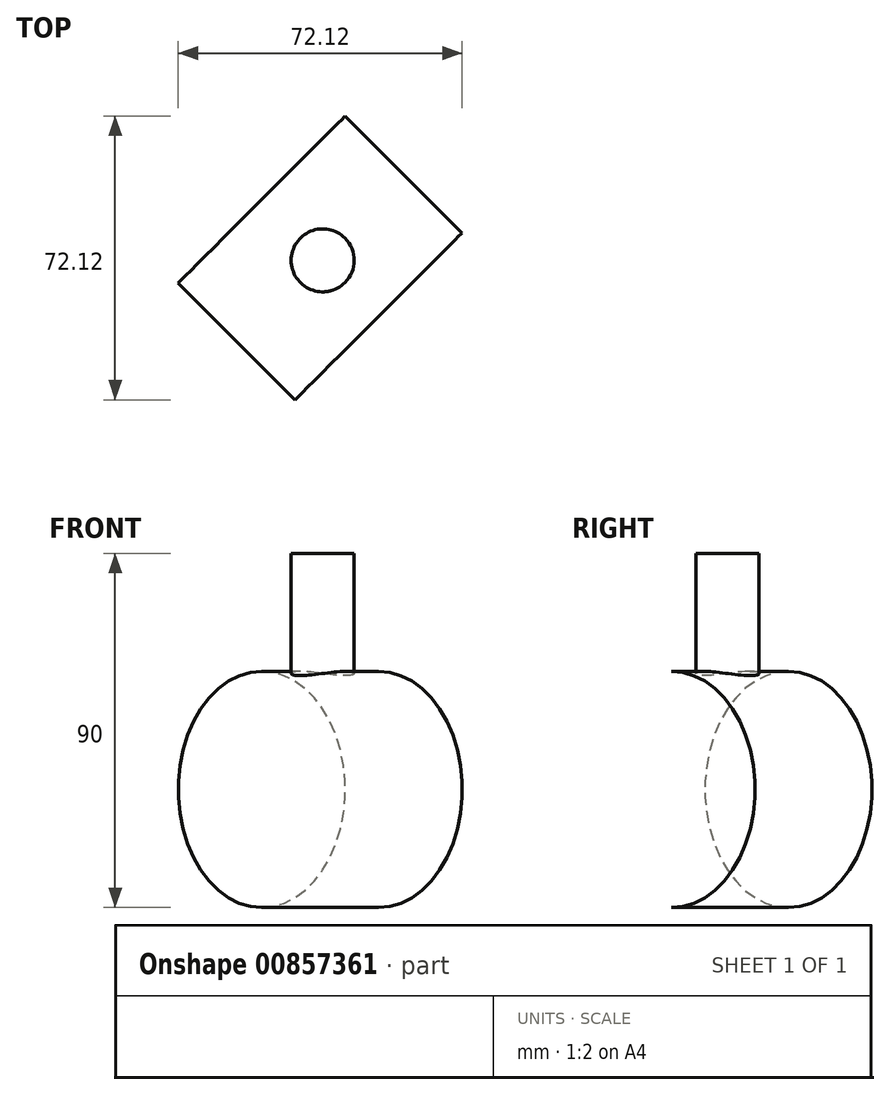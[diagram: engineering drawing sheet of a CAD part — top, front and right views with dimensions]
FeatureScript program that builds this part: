
annotation { "Feature Type Name" : "Feature", "Feature Type Description" : "" }
export const myFeature = defineFeature(function(context is Context, id is Id, definition is map)
    precondition{}
    {
        {
            var Q0;
            Q0=qCreatedBy(makeId("Front.planeOp"),FACE);
            var sketch = newSketch(context, id + "F0", { "sketchPlane" : qUnion([Q0])});
            skCircle(sketch, "E0", {"center": v(0, 0) * mm, "radius": 30 * mm});
            skSolve(sketch);
        }
        {
            var Q0;
            Q0=makeQuery(id+"F0.imprint","IMPRINT",FACE,{"disambiguationData":[TD([[makeQuery(id+"F0.imprint","IMPRINT",EDGE,{"derivedFrom":sQuery(id+"F0.wireOp",EDGE,"E0")}),1.0]])]});
            extrude(context, id + "F1", {"entities" : qUnion([Q0]), "depth" : 42 * mm, "offsetDistance" : 25 * mm});
        }
        {
            var Q0;
            Q0=qCreatedBy(makeId("Top.planeOp"),FACE);
            var sketch = newSketch(context, id + "F2", { "sketchPlane" : qUnion([Q0])});
            skCircle(sketch, "E1", {"center": v(0, -21.9) * mm, "radius": 8 * mm});
            skSolve(sketch);
        }
        {
            var Q0;
            Q0 = qSketchRegion(id + "F2", true);
            extrude(context, id + "F3", {"entities" : qUnion([Q0]), "operationType" : NewBodyOperationType.ADD, "depth" : 60 * mm, "offsetDistance" : 25 * mm});
        }
        {
            var Q0;
            Q0=makeQuery(id+"F1.opExtrude","SWEPT_BODY",BODY,{"disambiguationData":[OSD([sQuery(id+"F0.wireOp",EDGE,"E0")])]});
            var Q1;
            Q1=makeQuery(id+"F3.opExtrude","CAP_EDGE",EDGE,{"disambiguationData":[OSD([sQuery(id+"F2.wireOp",EDGE,"E1")])],"isStart":false});
            transform(context, id + "F4", {"entities" : qUnion([Q0]), "transformType" : TransformType.ROTATION, "transformAxis" : qUnion([Q1]), "angle" : 45 * degree, "makeCopy" : false});
        }
    });
